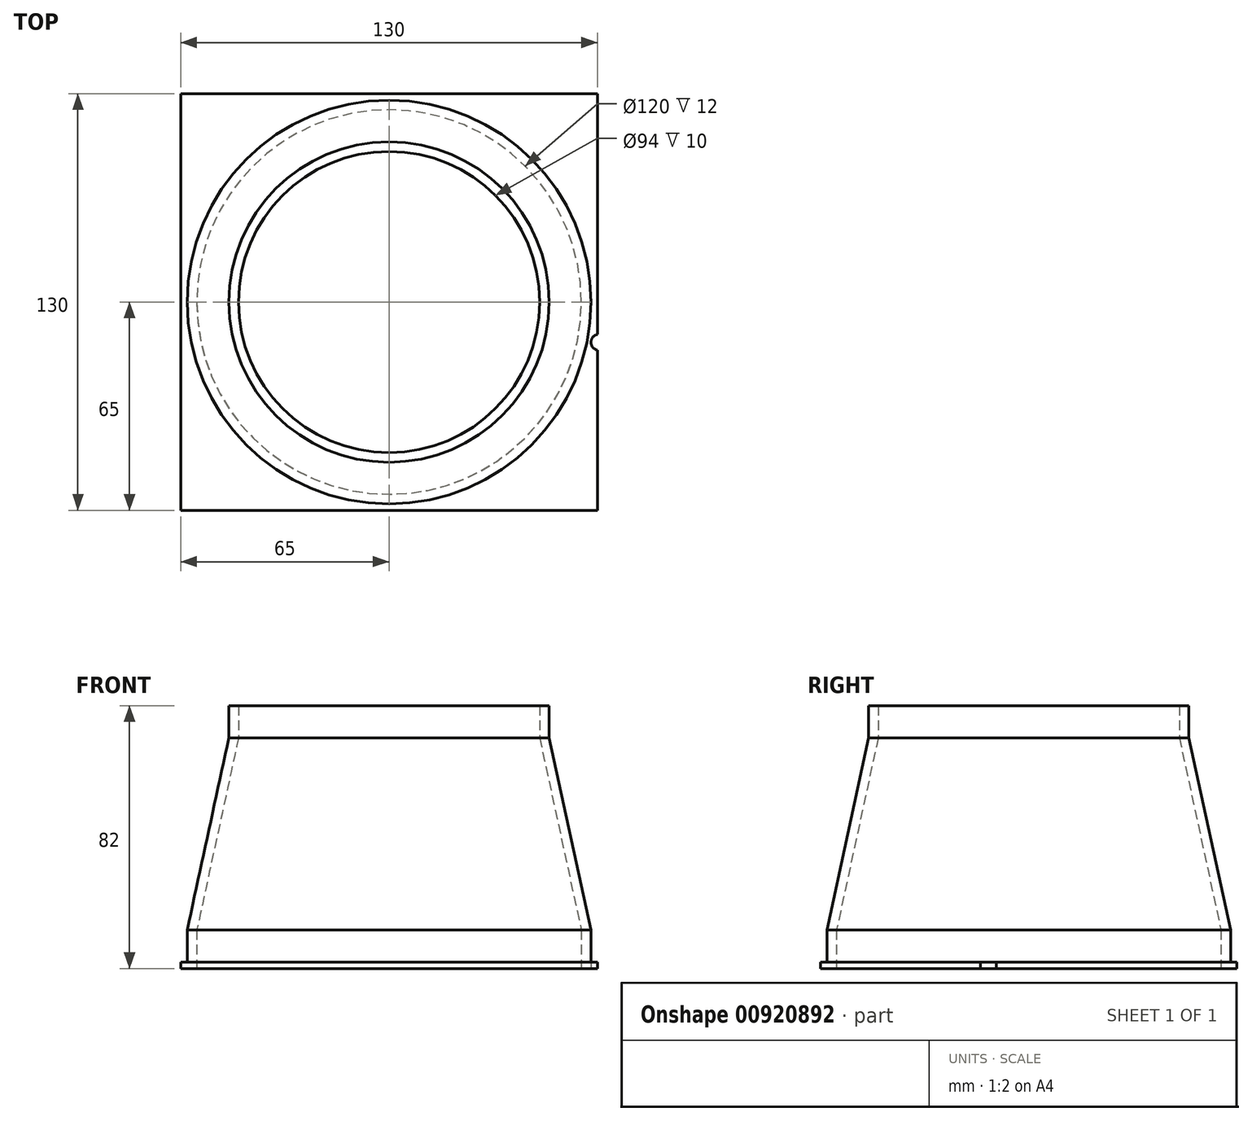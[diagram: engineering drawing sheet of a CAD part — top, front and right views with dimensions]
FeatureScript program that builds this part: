
annotation { "Feature Type Name" : "Feature", "Feature Type Description" : "" }
export const myFeature = defineFeature(function(context is Context, id is Id, definition is map)
    precondition{}
    {
        {
            var Q0;
            Q0=qCreatedBy(makeId("Top.planeOp"),FACE);
            var sketch = newSketch(context, id + "F0", { "sketchPlane" : qUnion([Q0])});
            skLineSegment(sketch, "E0.bottom", {"start": v(-65, 65) * mm, "end": v(65, 65) * mm});
            skLineSegment(sketch, "E0.top", {"start": v(-65, -65) * mm, "end": v(65, -65) * mm});
            skLineSegment(sketch, "E0.left", {"start": v(-65, 65) * mm, "end": v(-65, -65) * mm});
            skLineSegment(sketch, "E0.right", {"start": v(65, 65) * mm, "end": v(65, -65) * mm});
            skPoint(sketch, "E1", {"position": v(0, 65) * mm});
            skPoint(sketch, "E2", {"position": v(0, -65) * mm});
            skPoint(sketch, "E3", {"position": v(0, 0) * mm});
            skPoint(sketch, "E3.positionSnap0", {"position": v(-65, 0) * mm});
            skCircle(sketch, "E4", {"center": v(0, 0) * mm, "radius": 60 * mm});
            skCircle(sketch, "E5", {"center": v(-41.32, 92.61) * mm, "radius": 2.5 * mm});
            skCircle(sketch, "E6", {"center": v(65.52, 92.61) * mm, "radius": 2.5 * mm});
            skCircle(sketch, "E7", {"center": v(65.52, -12.57) * mm, "radius": 2.5 * mm});
            skCircle(sketch, "E8", {"center": v(-41.32, -12.57) * mm, "radius": 2.5 * mm});
            skCircle(sketch, "E9", {"center": v(0, 0) * mm, "radius": 63 * mm});
            skSolve(sketch);
        }
        {
            var Q0;
            Q0=makeQuery(id+"F0.imprint","IMPRINT",FACE,{"disambiguationData":[TD([[makeQuery(id+"F0.imprint","IMPRINT",EDGE,{"derivedFrom":sQuery(id+"F0.wireOp",EDGE,"E0.bottom")}),-1.0]])]});
            var Q1;
            Q1=makeQuery(id+"F0.imprint","IMPRINT",FACE,{"disambiguationData":[TD([[makeQuery(id+"F0.imprint","IMPRINT",EDGE,{"derivedFrom":sQuery(id+"F0.wireOp",EDGE,"E4")}),-1.0]])]});
            extrude(context, id + "F1", {"entities" : qUnion([Q0, Q1]), "depth" : 2 * mm, "offsetDistance" : 25 * mm});
        }
        {
            var Q0;
            Q0=makeQuery(id+"F0.imprint","IMPRINT",FACE,{"disambiguationData":[TD([[makeQuery(id+"F0.imprint","IMPRINT",EDGE,{"derivedFrom":sQuery(id+"F0.wireOp",EDGE,"E4")}),-1.0]])]});
            extrude(context, id + "F2", {"entities" : qUnion([Q0]), "operationType" : NewBodyOperationType.ADD, "depth" : 12 * mm, "offsetDistance" : 25 * mm});
        }
        {
            var Q0;
            Q0=qCreatedBy(makeId("Right.planeOp"),FACE);
            var sketch = newSketch(context, id + "F3", { "sketchPlane" : qUnion([Q0])});
            skLineSegment(sketch, "E10.0", {"start": v(-63, 12) * mm, "end": v(63, 12) * mm});
            skPoint(sketch, "E11", {"position": v(0, 12) * mm});
            skLineSegment(sketch, "E12", {"start": v(0, 12) * mm, "end": v(0, 72) * mm, "construction": true});
            skLineSegment(sketch, "E13", {"start": v(0, 72) * mm, "end": v(50, 72) * mm});
            skLineSegment(sketch, "E14", {"start": v(50, 72) * mm, "end": v(63, 12) * mm});
            skPoint(sketch, "E15", {"position": v(47, 72) * mm});
            skLineSegment(sketch, "E16", {"start": v(47, 72) * mm, "end": v(60, 12) * mm});
            skSolve(sketch);
        }
        {
            var Q0;
            {var subQ0=sQuery(id+"F3.wireOp",EDGE,"E14");Q0=makeQuery(id+"F3.imprint","IMPRINT",FACE,{"disambiguationData":[TD([[makeQuery(id+"F3.imprint","IMPRINT",EDGE,{"derivedFrom":subQ0}),-1.0]])]});}
            var Q1;
            Q1=sQuery(id+"F3.wireOp",EDGE,"E12");
            revolve(context, id + "F4", {"operationType" : NewBodyOperationType.ADD, "surfaceOperationType" : NewSurfaceOperationType.NEW, "entities" : qUnion([Q0]), "axis" : qUnion([Q1]), "revolveType" : RevolveType.FULL});
        }
        {
            var Q0;
            Q0=makeQuery(id+"F4.opRevolve","SWEPT_FACE",FACE,{"disambiguationData":[OSD([sQuery(id+"F3.wireOp",EDGE,"E13")])]});
            extrude(context, id + "F5", {"entities" : qUnion([Q0]), "operationType" : NewBodyOperationType.ADD, "depth" : 10 * mm, "offsetDistance" : 25 * mm});
        }
    });
